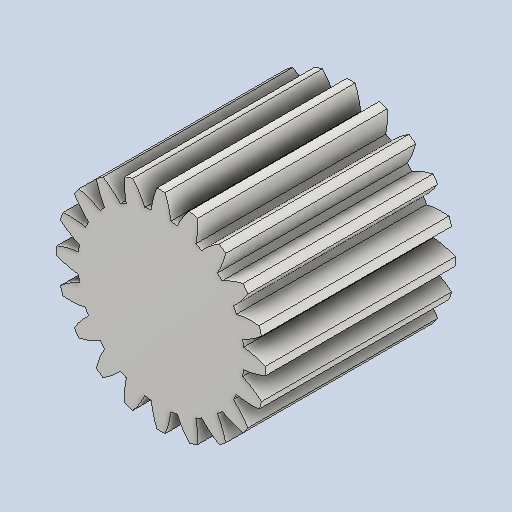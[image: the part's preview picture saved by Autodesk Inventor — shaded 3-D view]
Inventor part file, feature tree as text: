
AUTODESK INVENTOR PART (.ipt)
format: ipt  version: 2024 (Build 280153000, 153)  size: 267,776 bytes
history: native  units: mm (DEFAULTED — no unit token found)
features: plane x3, other x3, extrude x1, sketch x1
ambient origin geometry x8: Origin, YZ Plane, XZ Plane, XY Plane, X Axis, Y Axis, Z Axis, Center Point
bodies: Solid1 (feature_tree)
feature tree (8):
  extrude  "Extrusion1"  Depth=40.0mm TaperAngle=0.0deg
  plane  "Work Plane2"
  plane  "Work Plane8"
  plane  "Work Plane9"
  other  "Spur Gear"
  sketch  "Sketch1"  dims[d0=44.0mm d1=40.0mm d2=0.0mm d3=40.0mm d4=10.0mm d5=0.0mm d16=30.0mm d17=0.0mm d34=1.570796mm d39=0.0mm d41=0.0mm d43=30.0mm d46=30.0mm d47=0.0mm d48=0.0mm]
  other  "Srf1"
  other  "Pitch Diameter"
